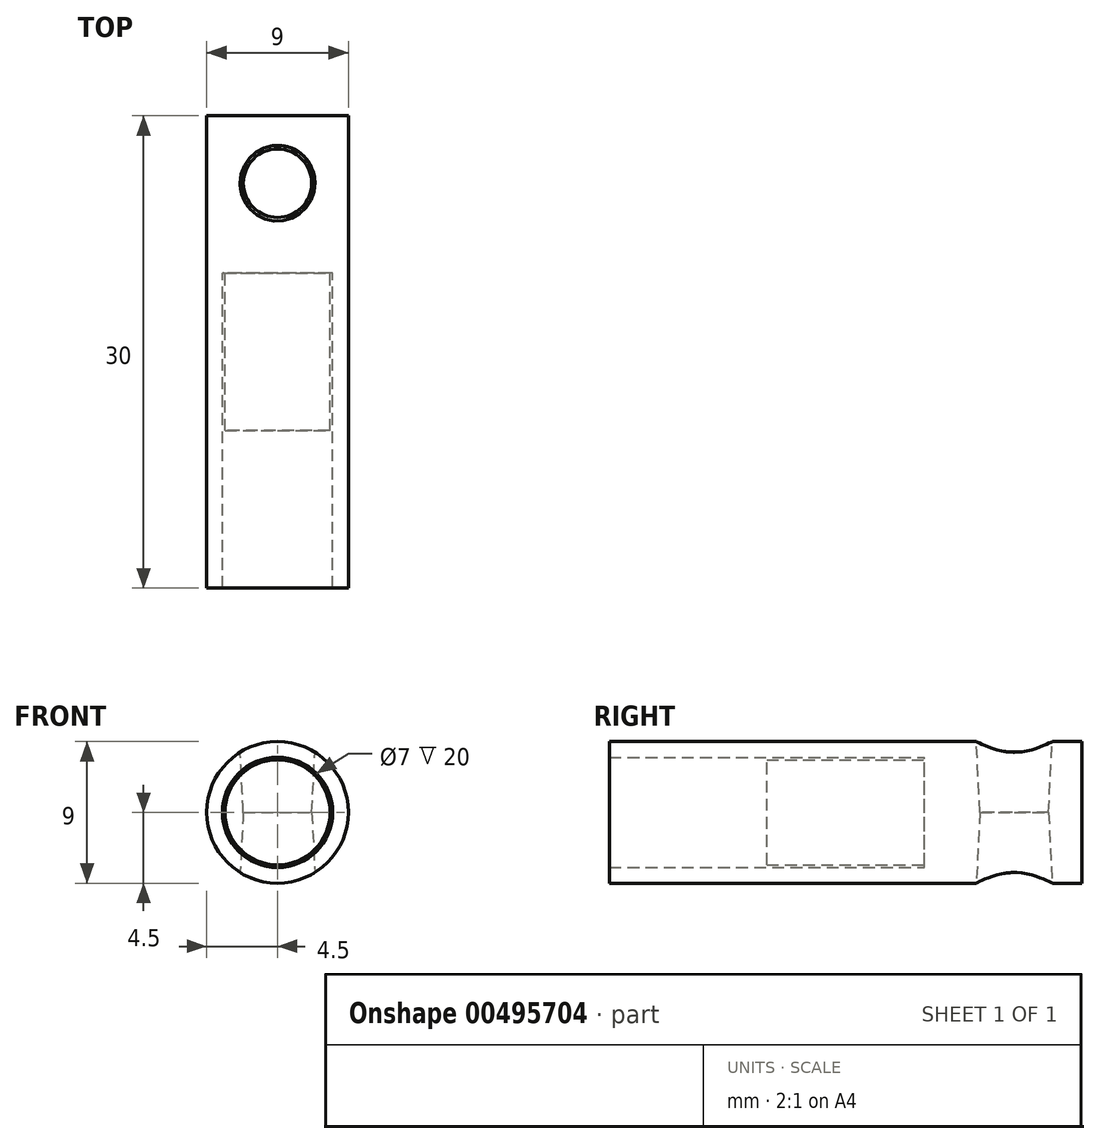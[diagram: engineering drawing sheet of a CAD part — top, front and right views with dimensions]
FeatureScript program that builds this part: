
annotation { "Feature Type Name" : "Feature", "Feature Type Description" : "" }
export const myFeature = defineFeature(function(context is Context, id is Id, definition is map)
    precondition{}
    {
        {
            var Q0;
            Q0=qCreatedBy(makeId("Front.planeOp"),FACE);
            var sketch = newSketch(context, id + "F0", { "sketchPlane" : qUnion([Q0])});
            skCircle(sketch, "E0", {"center": v(0, 0) * mm, "radius": 3.5 * mm});
            skSolve(sketch);
        }
        {
            var Q0;
            Q0=makeQuery(id+"F0.imprint","IMPRINT",FACE,{"disambiguationData":[TD([[makeQuery(id+"F0.imprint","IMPRINT",EDGE,{"derivedFrom":sQuery(id+"F0.wireOp",EDGE,"E0")}),1.0]])]});
            extrude(context, id + "F1", {"entities" : qUnion([Q0]), "depth" : 20 * mm, "offsetDistance" : 25 * mm});
        }
        {
            var Q0;
            Q0=makeQuery(id+"F1.opExtrude","CAP_FACE",FACE,{"disambiguationData":[OSD([sQuery(id+"F0.wireOp",EDGE,"E0")])],"isStart":false});
            shell(context, id + "F2", {"entities" : qUnion([Q0]), "thickness" : 1 * mm, "oppositeDirection" : true});
        }
        {
            var Q0;
            Q0=qCreatedBy(makeId("Front.planeOp"),FACE);
            var sketch = newSketch(context, id + "F3", { "sketchPlane" : qUnion([Q0])});
            skCircle(sketch, "E1", {"center": v(0, 0) * mm, "radius": 3.34 * mm});
            skSolve(sketch);
        }
        {
            var Q0;
            Q0 = qSketchRegion(id + "F3", true);
            extrude(context, id + "F4", {"entities" : qUnion([Q0]), "operationType" : NewBodyOperationType.ADD, "depth" : 10 * mm, "offsetDistance" : 25 * mm});
        }
        {
            var Q0;
            Q0=qCreatedBy(makeId("Front.planeOp"),FACE);
            var sketch = newSketch(context, id + "F5", { "sketchPlane" : qUnion([Q0])});
            skCircle(sketch, "E2", {"center": v(0, 0) * mm, "radius": 4.5 * mm});
            skSolve(sketch);
        }
        {
            var Q0;
            Q0 = qSketchRegion(id + "F5", true);
            extrude(context, id + "F6", {"entities" : qUnion([Q0]), "operationType" : NewBodyOperationType.ADD, "oppositeDirection" : true, "depth" : 10 * mm, "offsetDistance" : 25 * mm});
        }
        {
            var Q0;
            Q0=qCreatedBy(makeId("Top.planeOp"),FACE);
            var sketch = newSketch(context, id + "F7", { "sketchPlane" : qUnion([Q0])});
            skCircle(sketch, "E3", {"center": v(0, 5.71) * mm, "radius": 2.17 * mm});
            skCircle(sketch, "E4", {"center": v(0, 5.71) * mm, "radius": 1.5 * mm, "construction": true});
            skSolve(sketch);
        }
        {
            var Q0;
            Q0 = qSketchRegion(id + "F7", true);
            extrude(context, id + "F8", {"entities" : qUnion([Q0]), "operationType" : NewBodyOperationType.REMOVE, "endBound" : BoundingType.SYMMETRIC, "oppositeDirection" : true, "depth" : 30 * mm, "offsetDistance" : 25 * mm, "hasDraft" : true, "draftAngle" : 3 * degree});
        }
    });
